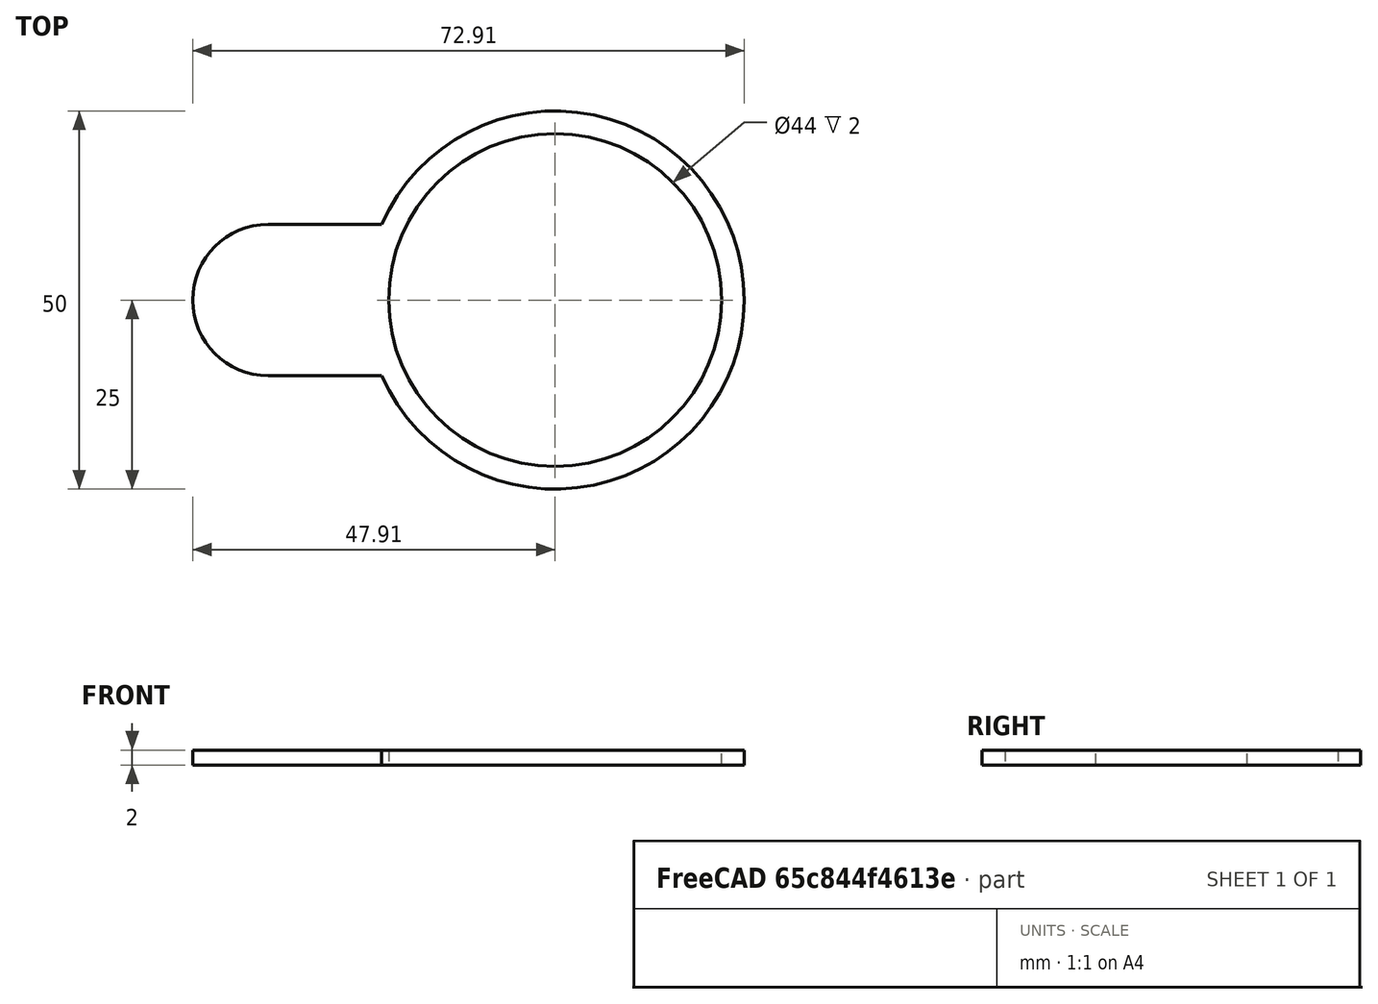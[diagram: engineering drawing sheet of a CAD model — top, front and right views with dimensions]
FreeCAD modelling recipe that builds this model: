
FCSTD DOCUMENT  (FreeCAD 0.21R33668 +26 (Git))
Label: plantilla pepperoni
License: All rights reserved
LicenseURL: https://en.wikipedia.org/wiki/All_rights_reserved
objects: Sketcher::SketchObject×1, PartDesign::Pad×1, PartDesign::Body×1
note: 4 computed .brp shape members not serialized (recipe doc carries the construction recipe); baked Part::Feature solids carry a one-line shape summary decoded from their .brp

FEATURE [Sketcher::SketchObject] Sketch
  FullyConstrained = true
  MapMode = 5
  Support = -> [XY_Plane]
  sketch-geometry (5):
    g0: Circle CenterX=0 CenterY=0 CenterZ=0 NormalX=0 NormalY=0 NormalZ=1 AngleXU=0 Radius=22
    g1: ArcOfCircle CenterX=0 CenterY=0 CenterZ=0 NormalX=0 NormalY=0 NormalZ=1 AngleXU=0 Radius=25 StartAngle=3.55311 EndAngle=9.01326
    g2: LineSegment StartX=-22.9129 StartY=-10 StartZ=0 EndX=-37.9129 EndY=-10 EndZ=0
    g3: ArcOfCircle CenterX=-37.9129 CenterY=4e-16 CenterZ=0 NormalX=0 NormalY=0 NormalZ=1 AngleXU=0 Radius=10 StartAngle=1.5708 EndAngle=4.71239
    g4: LineSegment StartX=-37.9129 StartY=10 StartZ=0 EndX=-22.9129 EndY=10 EndZ=0
  constraints (14):
    c: Coincident(g0,g-1)
    c: Diameter(g0) = 44
    c: Coincident(g1,g0)
    c: Diameter(g1) = 50
    c: Horizontal(g2)
    c: Coincident(g3,g2)
    c: Coincident(g4,g3)
    c: Horizontal(g4)
    c: DistanceX(g4,g4) = 15
    c: Symmetric(g3,g2,g-1)
    c: Radius(g3) = 10
    c: Coincident(g1,g4)
    c: Coincident(g1,g2)
    c: DistanceX(g3,g2) = 0
FEATURE [PartDesign::Pad] Pad
  Direction = (0,0,1)
  Length = 2
  Length2 = 10
  Profile = -> Sketch
  ReferenceAxis = -> Sketch [N_Axis]
  Type = 0
FEATURE [PartDesign::Body] Body  label="Cuerpo"
  Group = -> [Sketch,Pad]
  Origin = -> Origin
  Tip = -> Pad
